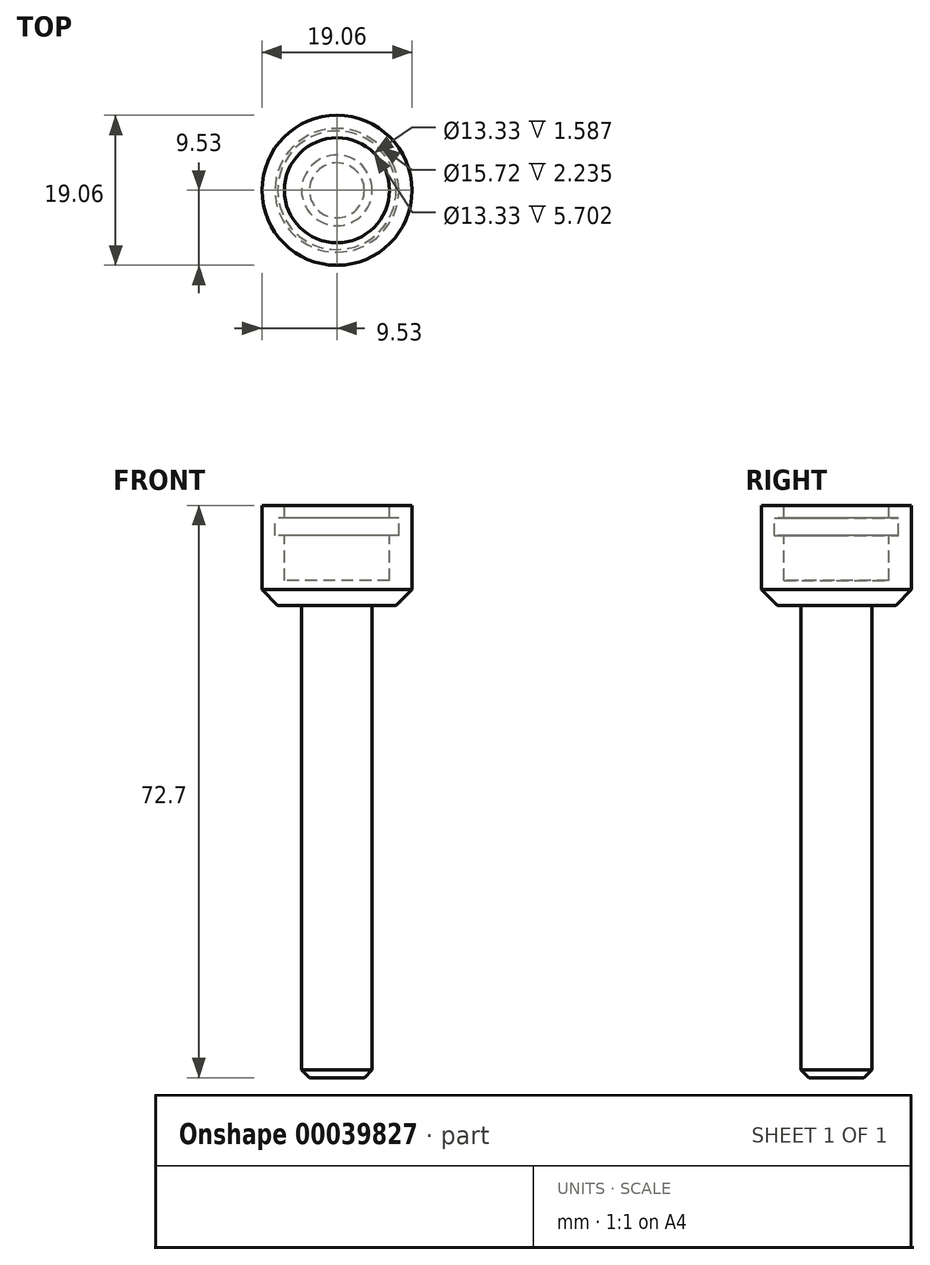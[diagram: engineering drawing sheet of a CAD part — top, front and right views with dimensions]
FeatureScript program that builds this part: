
annotation { "Feature Type Name" : "Feature", "Feature Type Description" : "" }
export const myFeature = defineFeature(function(context is Context, id is Id, definition is map)
    precondition{}
    {
        {
            var Q0;
            Q0=qCreatedBy(makeId("Top.planeOp"),FACE);
            var sketch = newSketch(context, id + "F0", { "sketchPlane" : qUnion([Q0])});
            skCircle(sketch, "E0", {"center": v(0, 0) * mm, "radius": 9.53 * mm});
            skSolve(sketch);
        }
        {
            var Q0;
            Q0=qSketchRegion(id+"F0",true);
            extrude(context, id + "F1", {"entities" : qUnion([Q0]), "depth" : 12.7 * mm});
        }
        {
            var Q0;
            Q0=makeQuery(id+"F1.opExtrude","CAP_FACE",FACE,{"disambiguationData":[OSD([sQuery(id+"F0.wireOp",EDGE,"E0")])],"isStart":false});
            var sketch = newSketch(context, id + "F2", { "sketchPlane" : qUnion([Q0])});
            skCircle(sketch, "E1", {"center": v(0, 0) * mm, "radius": 6.67 * mm});
            skSolve(sketch);
        }
        {
            var Q0;
            Q0=qSketchRegion(id+"F2",true);
            extrude(context, id + "F3", {"entities" : qUnion([Q0]), "operationType" : NewBodyOperationType.REMOVE, "oppositeDirection" : true, "depth" : 9.52 * mm});
        }
        {
            var Q0;
            Q0=qCreatedBy(makeId("Front.planeOp"),FACE);
            var sketch = newSketch(context, id + "F4", { "sketchPlane" : qUnion([Q0])});
            skLineSegment(sketch, "E2.bottom", {"start": v(6.67, 11.11) * mm, "end": v(7.86, 11.11) * mm});
            skLineSegment(sketch, "E2.top", {"start": v(6.67, 8.88) * mm, "end": v(7.86, 8.88) * mm});
            skLineSegment(sketch, "E2.left", {"start": v(6.67, 11.11) * mm, "end": v(6.67, 8.88) * mm});
            skLineSegment(sketch, "E2.right", {"start": v(7.86, 11.11) * mm, "end": v(7.86, 8.88) * mm});
            skLineSegment(sketch, "E3", {"start": v(0, 0) * mm, "end": v(0, 38.04) * mm, "construction": true});
            skSolve(sketch);
        }
        {
            var Q0;
            Q0=qSketchRegion(id+"F4",true);
            var Q1;
            Q1=sQuery(id+"F4.wireOp",EDGE,"E3");
            revolve(context, id + "F5", {"operationType" : NewBodyOperationType.REMOVE, "entities" : qUnion([Q0]), "axis" : qUnion([Q1]), "revolveType" : RevolveType.FULL, "oppositeDirection" : true});
        }
        {
            var Q0;
            Q0=makeQuery(id+"F1.opExtrude","CAP_FACE",FACE,{"disambiguationData":[OSD([sQuery(id+"F0.wireOp",EDGE,"E0")])],"isStart":true});
            var sketch = newSketch(context, id + "F6", { "sketchPlane" : qUnion([Q0])});
            skCircle(sketch, "E4", {"center": v(0, 0) * mm, "radius": 17.46 * mm});
            skSolve(sketch);
        }
        {
            var Q0;
            Q0=makeQuery(id+"F1.opExtrude","CAP_EDGE",EDGE,{"disambiguationData":[OSD([sQuery(id+"F0.wireOp",EDGE,"E0")])],"isStart":true});
            chamfer(context, id + "F7", {"entities" : qUnion([Q0]), "width" : 2 * mm, "tangentPropagation" : true});
        }
        {
            var Q0;
            Q0=makeQuery(id+"F1.opExtrude","CAP_FACE",FACE,{"disambiguationData":[OSD([sQuery(id+"F0.wireOp",EDGE,"E0")])],"isStart":true});
            var sketch = newSketch(context, id + "F8", { "sketchPlane" : qUnion([Q0])});
            skCircle(sketch, "E5", {"center": v(0, 0) * mm, "radius": 4.49 * mm});
            skSolve(sketch);
        }
        {
            var Q0;
            Q0 = qSketchRegion(id + "F8", true);
            extrude(context, id + "F9", {"entities" : qUnion([Q0]), "operationType" : NewBodyOperationType.ADD, "depth" : 60 * mm});
        }
        {
            var Q0;
            Q0=makeQuery(id+"F9.opExtrude","CAP_EDGE",EDGE,{"disambiguationData":[OSD([sQuery(id+"F8.wireOp",EDGE,"E5")])],"isStart":false});
            chamfer(context, id + "F10", {"entities" : qUnion([Q0]), "width" : 1 * mm, "tangentPropagation" : true});
        }
        {
            var Q0;
            Q0 = qConstructionFilter(qBodyType(qCreatedBy(id + "F8" ,EDGE), BodyType.WIRE), ConstructionObject.NO);
            extrude(context, id + "F11", {"bodyType" : ExtendedToolBodyType.SURFACE, "surfaceEntities" : qUnion([Q0]), "depth" : 65 * mm});
        }
    });
